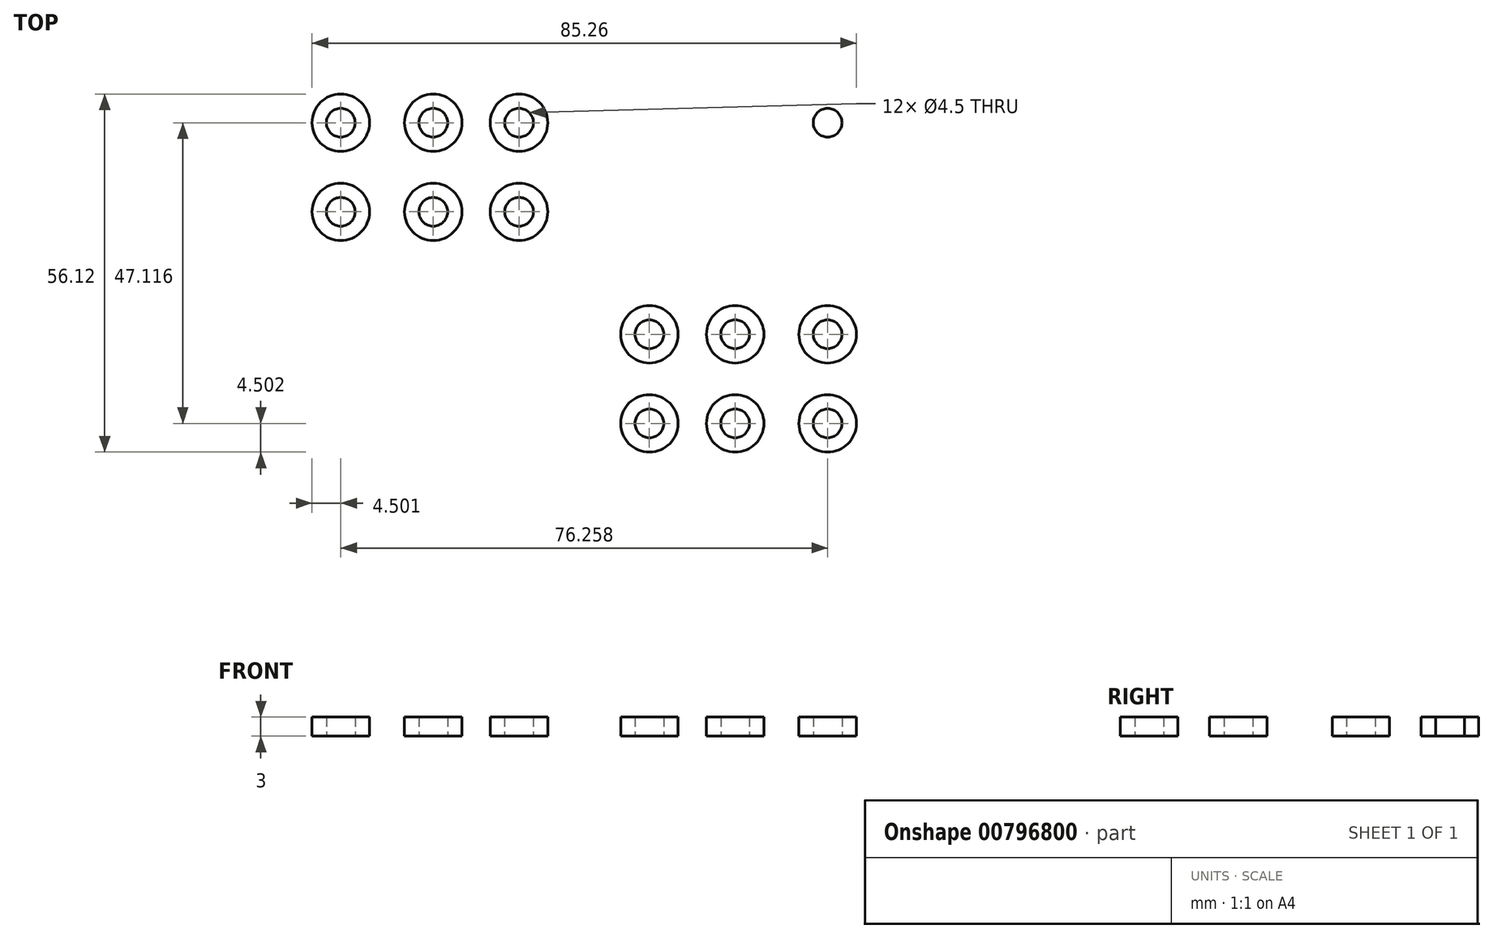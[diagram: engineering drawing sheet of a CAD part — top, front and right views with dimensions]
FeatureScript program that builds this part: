
annotation { "Feature Type Name" : "Feature", "Feature Type Description" : "" }
export const myFeature = defineFeature(function(context is Context, id is Id, definition is map)
    precondition{}
    {
        {
            var Q0;
            Q0=qCreatedBy(makeId("Top.planeOp"),FACE);
            var sketch = newSketch(context, id + "F0", { "sketchPlane" : qUnion([Q0])});
            skCircle(sketch, "E0", {"center": v(-10.2, 9.6) * mm, "radius": 4.5 * mm});
            skCircle(sketch, "E1", {"center": v(-10.2, 9.6) * mm, "radius": 2.25 * mm});
            skCircle(sketch, "E2", {"center": v(-23.65, 9.6) * mm, "radius": 4.5 * mm});
            skCircle(sketch, "E3", {"center": v(-23.65, 9.6) * mm, "radius": 2.25 * mm});
            skCircle(sketch, "E4", {"center": v(-38.13, 23.56) * mm, "radius": 4.5 * mm});
            skCircle(sketch, "E5", {"center": v(-38.13, 23.56) * mm, "radius": 2.25 * mm});
            skCircle(sketch, "E6", {"center": v(-10.2, 23.56) * mm, "radius": 2.25 * mm});
            skCircle(sketch, "E7", {"center": v(-10.2, 23.56) * mm, "radius": 4.5 * mm});
            skCircle(sketch, "E8", {"center": v(-23.65, 23.56) * mm, "radius": 2.25 * mm});
            skCircle(sketch, "E9", {"center": v(-23.65, 23.56) * mm, "radius": 4.5 * mm});
            skCircle(sketch, "E10", {"center": v(-38.13, 9.6) * mm, "radius": 2.25 * mm});
            skCircle(sketch, "E11", {"center": v(-38.13, 9.6) * mm, "radius": 4.5 * mm});
            skCircle(sketch, "E12.MirrorC", {"center": v(-10.2, -9.6) * mm, "radius": 4.5 * mm});
            skCircle(sketch, "E13.MirrorC", {"center": v(-10.2, -9.6) * mm, "radius": 2.25 * mm});
            skCircle(sketch, "E14.MirrorC", {"center": v(-23.65, -9.6) * mm, "radius": 4.5 * mm});
            skCircle(sketch, "E15.MirrorC", {"center": v(-38.13, -9.6) * mm, "radius": 4.5 * mm});
            skCircle(sketch, "E16.MirrorC", {"center": v(-38.13, -23.56) * mm, "radius": 4.5 * mm});
            skCircle(sketch, "E17.MirrorC", {"center": v(-23.65, -9.6) * mm, "radius": 2.25 * mm});
            skCircle(sketch, "E18.MirrorC", {"center": v(-38.13, -9.6) * mm, "radius": 2.25 * mm});
            skCircle(sketch, "E19.MirrorC", {"center": v(-38.13, -23.56) * mm, "radius": 2.25 * mm});
            skCircle(sketch, "E20.MirrorC", {"center": v(-10.2, -23.56) * mm, "radius": 4.5 * mm});
            skCircle(sketch, "E21.MirrorC", {"center": v(-23.65, -23.56) * mm, "radius": 4.5 * mm});
            skCircle(sketch, "E22.MirrorC", {"center": v(-10.2, -23.56) * mm, "radius": 2.25 * mm});
            skCircle(sketch, "E23.MirrorC", {"center": v(-23.65, -23.56) * mm, "radius": 2.25 * mm});
            skCircle(sketch, "E24.MirrorC", {"center": v(38.13, -23.56) * mm, "radius": 4.5 * mm});
            skCircle(sketch, "E25.MirrorC", {"center": v(38.13, -9.6) * mm, "radius": 2.25 * mm});
            skCircle(sketch, "E26.MirrorC", {"center": v(10.2, -23.56) * mm, "radius": 4.5 * mm});
            skCircle(sketch, "E27.MirrorC", {"center": v(10.2, -23.56) * mm, "radius": 2.25 * mm});
            skCircle(sketch, "E28.MirrorC", {"center": v(23.65, -23.56) * mm, "radius": 2.25 * mm});
            skCircle(sketch, "E29.MirrorC", {"center": v(10.2, -9.6) * mm, "radius": 4.5 * mm});
            skCircle(sketch, "E30.MirrorC", {"center": v(38.13, 9.6) * mm, "radius": 4.5 * mm});
            skCircle(sketch, "E31.MirrorC", {"center": v(38.13, 9.6) * mm, "radius": 2.25 * mm});
            skCircle(sketch, "E32.MirrorC", {"center": v(23.65, 23.56) * mm, "radius": 4.5 * mm});
            skCircle(sketch, "E33.MirrorC", {"center": v(23.65, 23.56) * mm, "radius": 2.25 * mm});
            skCircle(sketch, "E34.MirrorC", {"center": v(10.2, 23.56) * mm, "radius": 4.5 * mm});
            skCircle(sketch, "E35.MirrorC", {"center": v(10.2, 23.56) * mm, "radius": 2.25 * mm});
            skCircle(sketch, "E36.MirrorC", {"center": v(38.13, 23.56) * mm, "radius": 2.25 * mm});
            skCircle(sketch, "E37.MirrorC", {"center": v(38.13, 23.56) * mm, "radius": 4.5 * mm});
            skCircle(sketch, "E38.MirrorC", {"center": v(23.65, -23.56) * mm, "radius": 4.5 * mm});
            skCircle(sketch, "E39.MirrorC", {"center": v(38.13, -23.56) * mm, "radius": 2.25 * mm});
            skCircle(sketch, "E40.MirrorC", {"center": v(23.65, 9.6) * mm, "radius": 4.5 * mm});
            skCircle(sketch, "E41.MirrorC", {"center": v(23.65, 9.6) * mm, "radius": 2.25 * mm});
            skCircle(sketch, "E42.MirrorC", {"center": v(23.65, -9.6) * mm, "radius": 2.25 * mm});
            skCircle(sketch, "E43.MirrorC", {"center": v(10.2, -9.6) * mm, "radius": 2.25 * mm});
            skCircle(sketch, "E44.MirrorC", {"center": v(38.13, -9.6) * mm, "radius": 4.5 * mm});
            skCircle(sketch, "E45.MirrorC", {"center": v(10.2, 9.6) * mm, "radius": 4.5 * mm});
            skCircle(sketch, "E46.MirrorC", {"center": v(10.2, 9.6) * mm, "radius": 2.25 * mm});
            skCircle(sketch, "E47.MirrorC", {"center": v(23.65, -9.6) * mm, "radius": 4.5 * mm});
            skSolve(sketch);
        }
        {
            var Q0;
            Q0=makeQuery(id+"F0.imprint","IMPRINT",FACE,{"disambiguationData":[TD([[makeQuery(id+"F0.imprint","IMPRINT",EDGE,{"derivedFrom":sQuery(id+"F0.wireOp",EDGE,"E4")}),1.0]])]});
            var Q1;
            Q1=makeQuery(id+"F0.imprint","IMPRINT",FACE,{"disambiguationData":[TD([[makeQuery(id+"F0.imprint","IMPRINT",EDGE,{"derivedFrom":sQuery(id+"F0.wireOp",EDGE,"E8")}),-1.0]])]});
            var Q2;
            Q2=makeQuery(id+"F0.imprint","IMPRINT",FACE,{"disambiguationData":[TD([[makeQuery(id+"F0.imprint","IMPRINT",EDGE,{"derivedFrom":sQuery(id+"F0.wireOp",EDGE,"E6")}),-1.0]])]});
            var Q3;
            Q3=makeQuery(id+"F0.imprint","IMPRINT",FACE,{"disambiguationData":[TD([[makeQuery(id+"F0.imprint","IMPRINT",EDGE,{"derivedFrom":sQuery(id+"F0.wireOp",EDGE,"E0")}),1.0]])]});
            var Q4;
            Q4=makeQuery(id+"F0.imprint","IMPRINT",FACE,{"disambiguationData":[TD([[makeQuery(id+"F0.imprint","IMPRINT",EDGE,{"derivedFrom":sQuery(id+"F0.wireOp",EDGE,"E2")}),1.0]])]});
            var Q5;
            Q5=makeQuery(id+"F0.imprint","IMPRINT",FACE,{"disambiguationData":[TD([[makeQuery(id+"F0.imprint","IMPRINT",EDGE,{"derivedFrom":sQuery(id+"F0.wireOp",EDGE,"E10")}),-1.0]])]});
            var Q6;
            Q6=makeQuery(id+"F0.imprint","IMPRINT",FACE,{"disambiguationData":[TD([[makeQuery(id+"F0.imprint","IMPRINT",EDGE,{"derivedFrom":sQuery(id+"F0.wireOp",EDGE,"E14.MirrorC")}),-1.0]])]});
            var Q7;
            Q7=makeQuery(id+"F0.imprint","IMPRINT",FACE,{"disambiguationData":[TD([[makeQuery(id+"F0.imprint","IMPRINT",EDGE,{"derivedFrom":sQuery(id+"F0.wireOp",EDGE,"E15.MirrorC")}),-1.0]])]});
            var Q8;
            Q8=makeQuery(id+"F0.imprint","IMPRINT",FACE,{"disambiguationData":[TD([[makeQuery(id+"F0.imprint","IMPRINT",EDGE,{"derivedFrom":sQuery(id+"F0.wireOp",EDGE,"E16.MirrorC")}),-1.0]])]});
            var Q9;
            Q9=makeQuery(id+"F0.imprint","IMPRINT",FACE,{"disambiguationData":[TD([[makeQuery(id+"F0.imprint","IMPRINT",EDGE,{"derivedFrom":sQuery(id+"F0.wireOp",EDGE,"E21.MirrorC")}),-1.0]])]});
            var Q10;
            Q10=makeQuery(id+"F0.imprint","IMPRINT",FACE,{"disambiguationData":[TD([[makeQuery(id+"F0.imprint","IMPRINT",EDGE,{"derivedFrom":sQuery(id+"F0.wireOp",EDGE,"E20.MirrorC")}),-1.0]])]});
            var Q11;
            Q11=makeQuery(id+"F0.imprint","IMPRINT",FACE,{"disambiguationData":[TD([[makeQuery(id+"F0.imprint","IMPRINT",EDGE,{"derivedFrom":sQuery(id+"F0.wireOp",EDGE,"E12.MirrorC")}),-1.0]])]});
            var Q12;
            Q12=makeQuery(id+"F0.imprint","IMPRINT",FACE,{"disambiguationData":[TD([[makeQuery(id+"F0.imprint","IMPRINT",EDGE,{"derivedFrom":sQuery(id+"F0.wireOp",EDGE,"E34.MirrorC")}),-1.0]])]});
            var Q13;
            Q13=makeQuery(id+"F0.imprint","IMPRINT",FACE,{"disambiguationData":[TD([[makeQuery(id+"F0.imprint","IMPRINT",EDGE,{"derivedFrom":sQuery(id+"F0.wireOp",EDGE,"E45.MirrorC")}),-1.0]])]});
            var Q14;
            Q14=makeQuery(id+"F0.imprint","IMPRINT",FACE,{"disambiguationData":[TD([[makeQuery(id+"F0.imprint","IMPRINT",EDGE,{"derivedFrom":sQuery(id+"F0.wireOp",EDGE,"E29.MirrorC")}),1.0]])]});
            var Q15;
            Q15=makeQuery(id+"F0.imprint","IMPRINT",FACE,{"disambiguationData":[TD([[makeQuery(id+"F0.imprint","IMPRINT",EDGE,{"derivedFrom":sQuery(id+"F0.wireOp",EDGE,"E26.MirrorC")}),1.0]])]});
            var Q16;
            Q16=makeQuery(id+"F0.imprint","IMPRINT",FACE,{"disambiguationData":[TD([[makeQuery(id+"F0.imprint","IMPRINT",EDGE,{"derivedFrom":sQuery(id+"F0.wireOp",EDGE,"E42.MirrorC")}),-1.0]])]});
            var Q17;
            Q17=makeQuery(id+"F0.imprint","IMPRINT",FACE,{"disambiguationData":[TD([[makeQuery(id+"F0.imprint","IMPRINT",EDGE,{"derivedFrom":sQuery(id+"F0.wireOp",EDGE,"E28.MirrorC")}),-1.0]])]});
            var Q18;
            Q18=makeQuery(id+"F0.imprint","IMPRINT",FACE,{"disambiguationData":[TD([[makeQuery(id+"F0.imprint","IMPRINT",EDGE,{"derivedFrom":sQuery(id+"F0.wireOp",EDGE,"E25.MirrorC")}),-1.0]])]});
            var Q19;
            Q19=makeQuery(id+"F0.imprint","IMPRINT",FACE,{"disambiguationData":[TD([[makeQuery(id+"F0.imprint","IMPRINT",EDGE,{"derivedFrom":sQuery(id+"F0.wireOp",EDGE,"E24.MirrorC")}),1.0]])]});
            var Q20;
            Q20=makeQuery(id+"F0.imprint","IMPRINT",FACE,{"disambiguationData":[TD([[makeQuery(id+"F0.imprint","IMPRINT",EDGE,{"derivedFrom":sQuery(id+"F0.wireOp",EDGE,"E30.MirrorC")}),-1.0]])]});
            var Q21;
            Q21=makeQuery(id+"F0.imprint","IMPRINT",FACE,{"disambiguationData":[TD([[makeQuery(id+"F0.imprint","IMPRINT",EDGE,{"derivedFrom":sQuery(id+"F0.wireOp",EDGE,"E40.MirrorC")}),-1.0]])]});
            var Q22;
            Q22=makeQuery(id+"F0.imprint","IMPRINT",FACE,{"disambiguationData":[TD([[makeQuery(id+"F0.imprint","IMPRINT",EDGE,{"derivedFrom":sQuery(id+"F0.wireOp",EDGE,"E32.MirrorC")}),-1.0]])]});
            var Q23;
            Q23=makeQuery(id+"F0.imprint","IMPRINT",FACE,{"disambiguationData":[TD([[makeQuery(id+"F0.imprint","IMPRINT",EDGE,{"derivedFrom":sQuery(id+"F0.wireOp",EDGE,"E36.MirrorC")}),1.0]])]});
            extrude(context, id + "F1", {"entities" : qUnion([Q0, Q1, Q2, Q3, Q4, Q5, Q6, Q7, Q8, Q9, Q10, Q11, Q12, Q13, Q14, Q15, Q16, Q17, Q18, Q19, Q20, Q21, Q22, Q23]), "depth" : 3 * mm, "offsetDistance" : 25 * mm});
        }
    });
